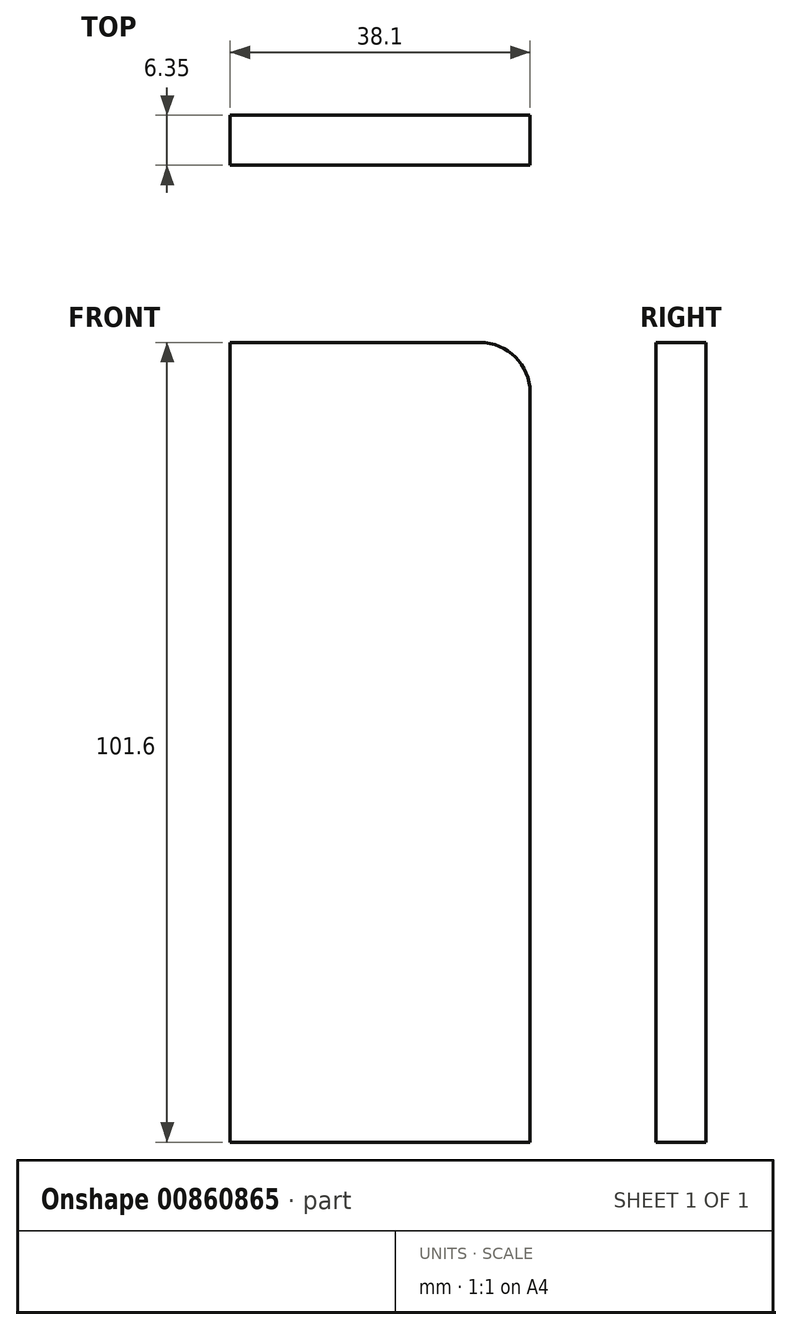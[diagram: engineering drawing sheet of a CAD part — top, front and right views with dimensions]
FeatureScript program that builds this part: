
annotation { "Feature Type Name" : "Feature", "Feature Type Description" : "" }
export const myFeature = defineFeature(function(context is Context, id is Id, definition is map)
    precondition{}
    {
        {
            var Q0;
            Q0=qCreatedBy(makeId("Front.planeOp"),FACE);
            var sketch = newSketch(context, id + "F0", { "sketchPlane" : qUnion([Q0])});
            skLineSegment(sketch, "E0.bottom", {"start": v(-38.36, 61.45) * mm, "end": v(-6.61, 61.45) * mm});
            skLineSegment(sketch, "E0.top", {"start": v(-38.36, -40.15) * mm, "end": v(-0.26, -40.15) * mm});
            skLineSegment(sketch, "E0.left", {"start": v(-38.36, 61.45) * mm, "end": v(-38.36, -40.15) * mm});
            skLineSegment(sketch, "E0.right", {"start": v(-0.26, 55.1) * mm, "end": v(-0.26, -40.15) * mm});
            skPoint(sketch, "E1.visualSharp", {"position": v(-0.26, 61.45) * mm});
            skArc(sketch, "E1.filletArc", {"start": v(-0.26, 55.1) * mm, "mid": v(-2.12, 59.59) * mm, "end": v(-6.61, 61.45) * mm});
            skSolve(sketch);
        }
        {
            var Q0;
            Q0 = qSketchRegion(id + "F0", true);
            extrude(context, id + "F1", {"entities" : qUnion([Q0]), "depth" : 6.35 * mm, "offsetDistance" : 25.4 * mm});
        }
    });
